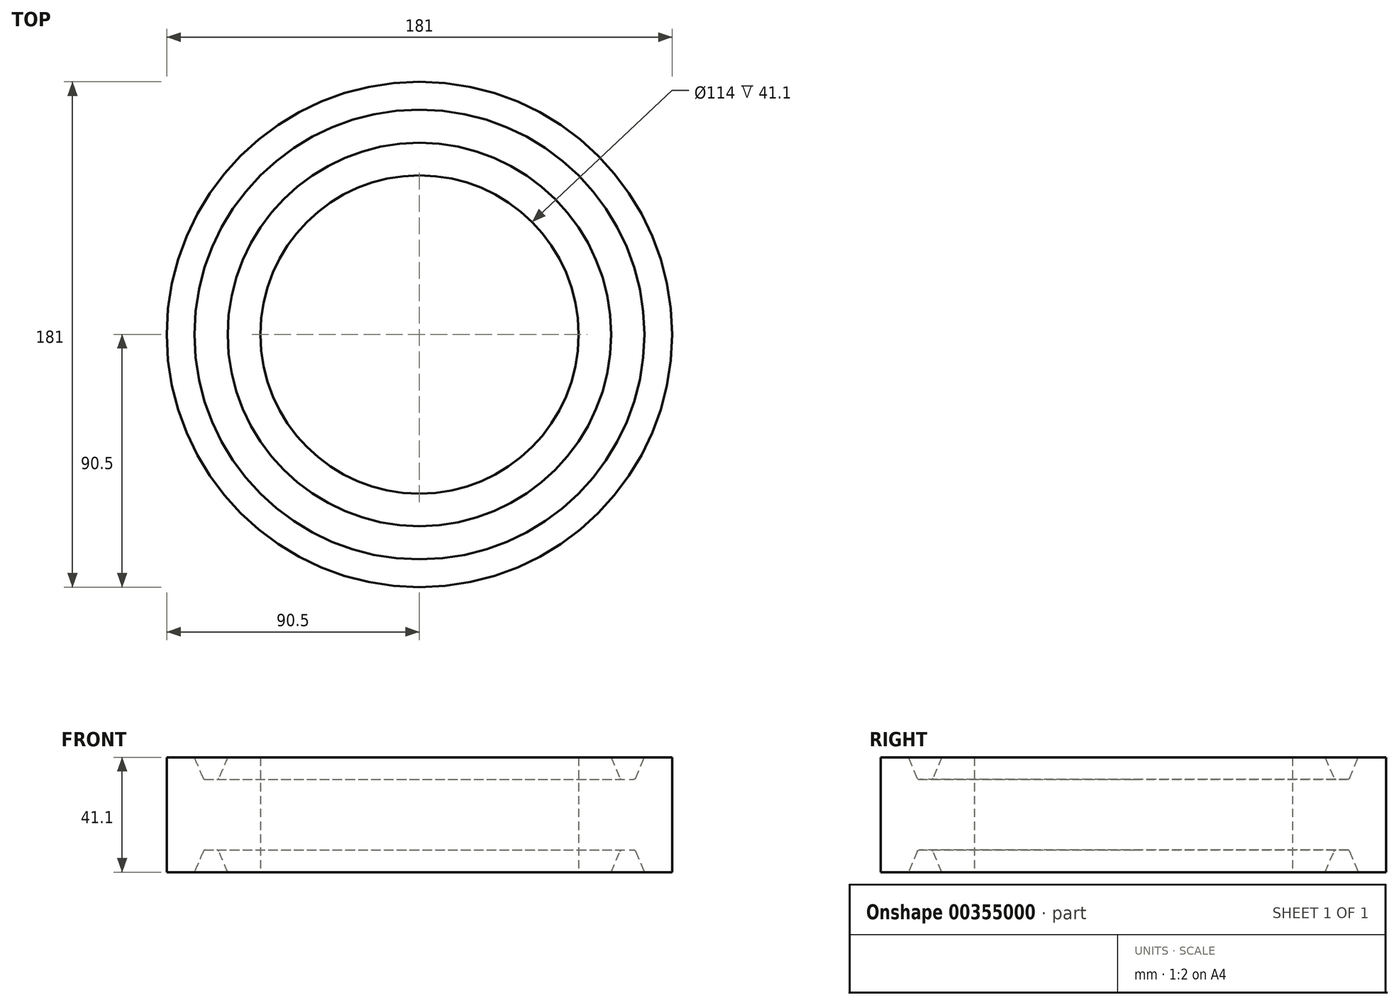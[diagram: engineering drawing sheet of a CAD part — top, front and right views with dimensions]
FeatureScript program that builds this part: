
annotation { "Feature Type Name" : "Feature", "Feature Type Description" : "" }
export const myFeature = defineFeature(function(context is Context, id is Id, definition is map)
    precondition{}
    {
        {
            var Q0;
            Q0=qCreatedBy(makeId("Top.planeOp"),FACE);
            var sketch = newSketch(context, id + "F0", { "sketchPlane" : qUnion([Q0])});
            skCircle(sketch, "E0", {"center": v(117.5, 0) * mm, "radius": 90.5 * mm});
            skCircle(sketch, "E1", {"center": v(117.5, 0) * mm, "radius": 57 * mm});
            skSolve(sketch);
        }
        {
            var Q0;
            Q0=makeQuery(id+"F0.imprint","IMPRINT",FACE,{"disambiguationData":[TD([[makeQuery(id+"F0.imprint","IMPRINT",EDGE,{"derivedFrom":sQuery(id+"F0.wireOp",EDGE,"E0")}),1.0]])]});
            extrude(context, id + "F1", {"entities" : qUnion([Q0]), "depth" : 41.1 * mm});
        }
        {
            var Q0;
            Q0=qCreatedBy(makeId("Front.planeOp"),FACE);
            var sketch = newSketch(context, id + "F2", { "sketchPlane" : qUnion([Q0])});
            skLineSegment(sketch, "E2", {"start": v(48.84, 41.1) * mm, "end": v(45.69, 33.67) * mm});
            skLineSegment(sketch, "E3", {"start": v(40.82, 33.18) * mm, "end": v(44.95, 33.18) * mm});
            skLineSegment(sketch, "E4", {"start": v(40.08, 33.67) * mm, "end": v(36.93, 41.1) * mm});
            skLineSegment(sketch, "E5", {"start": v(42.89, 33.18) * mm, "end": v(42.89, 41.1) * mm, "construction": true});
            skLineSegment(sketch, "E6", {"start": v(117.5, 41.1) * mm, "end": v(117.5, 0) * mm, "construction": true});
            skPoint(sketch, "E7.visualSharp", {"position": v(40.3, 33.18) * mm});
            skArc(sketch, "E7.filletArc", {"start": v(40.08, 33.67) * mm, "mid": v(40.38, 33.31) * mm, "end": v(40.82, 33.18) * mm});
            skPoint(sketch, "E8.visualSharp", {"position": v(45.48, 33.18) * mm});
            skArc(sketch, "E8.filletArc", {"start": v(44.95, 33.18) * mm, "mid": v(45.4, 33.31) * mm, "end": v(45.69, 33.67) * mm});
            skLineSegment(sketch, "E9", {"start": v(36.93, 41.1) * mm, "end": v(48.84, 41.1) * mm});
            skPoint(sketch, "E10", {"position": v(117.5, 20.55) * mm});
            skLineSegment(sketch, "E11", {"start": v(73.55, 20.55) * mm, "end": v(161.45, 20.55) * mm, "construction": true});
            skArc(sketch, "E12.MirrorCS", {"start": v(40.82, 33.18) * mm, "mid": v(40.38, 33.31) * mm, "end": v(40.08, 33.67) * mm});
            skArc(sketch, "E13.MirrorCS", {"start": v(45.69, 33.67) * mm, "mid": v(45.4, 33.31) * mm, "end": v(44.95, 33.18) * mm});
            skLineSegment(sketch, "E14.MirrorCS", {"start": v(44.95, 33.18) * mm, "end": v(40.82, 33.18) * mm});
            skLineSegment(sketch, "E15.MirrorCS", {"start": v(45.69, 33.67) * mm, "end": v(48.84, 41.1) * mm});
            skLineSegment(sketch, "E16.MirrorCS", {"start": v(36.93, 41.1) * mm, "end": v(40.08, 33.67) * mm});
            skLineSegment(sketch, "E17.MirrorCS", {"start": v(48.84, 41.1) * mm, "end": v(36.93, 41.1) * mm});
            skArc(sketch, "E18.MirrorCS", {"start": v(44.95, 7.92) * mm, "mid": v(45.4, 7.79) * mm, "end": v(45.69, 7.43) * mm});
            skArc(sketch, "E19.MirrorCS", {"start": v(40.08, 7.43) * mm, "mid": v(40.38, 7.79) * mm, "end": v(40.82, 7.92) * mm});
            skArc(sketch, "E20.MirrorCS", {"start": v(40.82, 7.92) * mm, "mid": v(40.38, 7.79) * mm, "end": v(40.08, 7.43) * mm});
            skArc(sketch, "E21.MirrorCS", {"start": v(45.69, 7.43) * mm, "mid": v(45.4, 7.79) * mm, "end": v(44.95, 7.92) * mm});
            skLineSegment(sketch, "E22.MirrorCS", {"start": v(44.95, 7.92) * mm, "end": v(40.82, 7.92) * mm});
            skPoint(sketch, "E23.MirrorP", {"position": v(45.48, 7.92) * mm});
            skPoint(sketch, "E24.MirrorP", {"position": v(40.3, 7.92) * mm});
            skLineSegment(sketch, "E25.MirrorCS", {"start": v(40.82, 7.92) * mm, "end": v(44.95, 7.92) * mm});
            skLineSegment(sketch, "E26.MirrorCS", {"start": v(36.93, 0) * mm, "end": v(48.84, 0) * mm});
            skLineSegment(sketch, "E27.MirrorCS", {"start": v(36.93, 0) * mm, "end": v(40.08, 7.43) * mm});
            skLineSegment(sketch, "E28.MirrorCS", {"start": v(45.69, 7.43) * mm, "end": v(48.84, 0) * mm});
            skLineSegment(sketch, "E29.MirrorCS", {"start": v(42.89, 7.92) * mm, "end": v(42.89, 0) * mm, "construction": true});
            skLineSegment(sketch, "E30.MirrorCS", {"start": v(40.08, 7.43) * mm, "end": v(36.93, 0) * mm});
            skLineSegment(sketch, "E31.MirrorCS", {"start": v(48.84, 0) * mm, "end": v(45.69, 7.43) * mm});
            skLineSegment(sketch, "E32.MirrorCS", {"start": v(48.84, 0) * mm, "end": v(36.93, 0) * mm});
            skSolve(sketch);
        }
        {
            var Q0;
            Q0=qSketchRegion(id+"F2",true);
            var Q1;
            Q1=sQuery(id+"F2.wireOp",EDGE,"E6");
            revolve(context, id + "F3", {"operationType" : NewBodyOperationType.REMOVE, "entities" : qUnion([Q0]), "axis" : qUnion([Q1]), "revolveType" : RevolveType.FULL, "oppositeDirection" : true});
        }
    });
